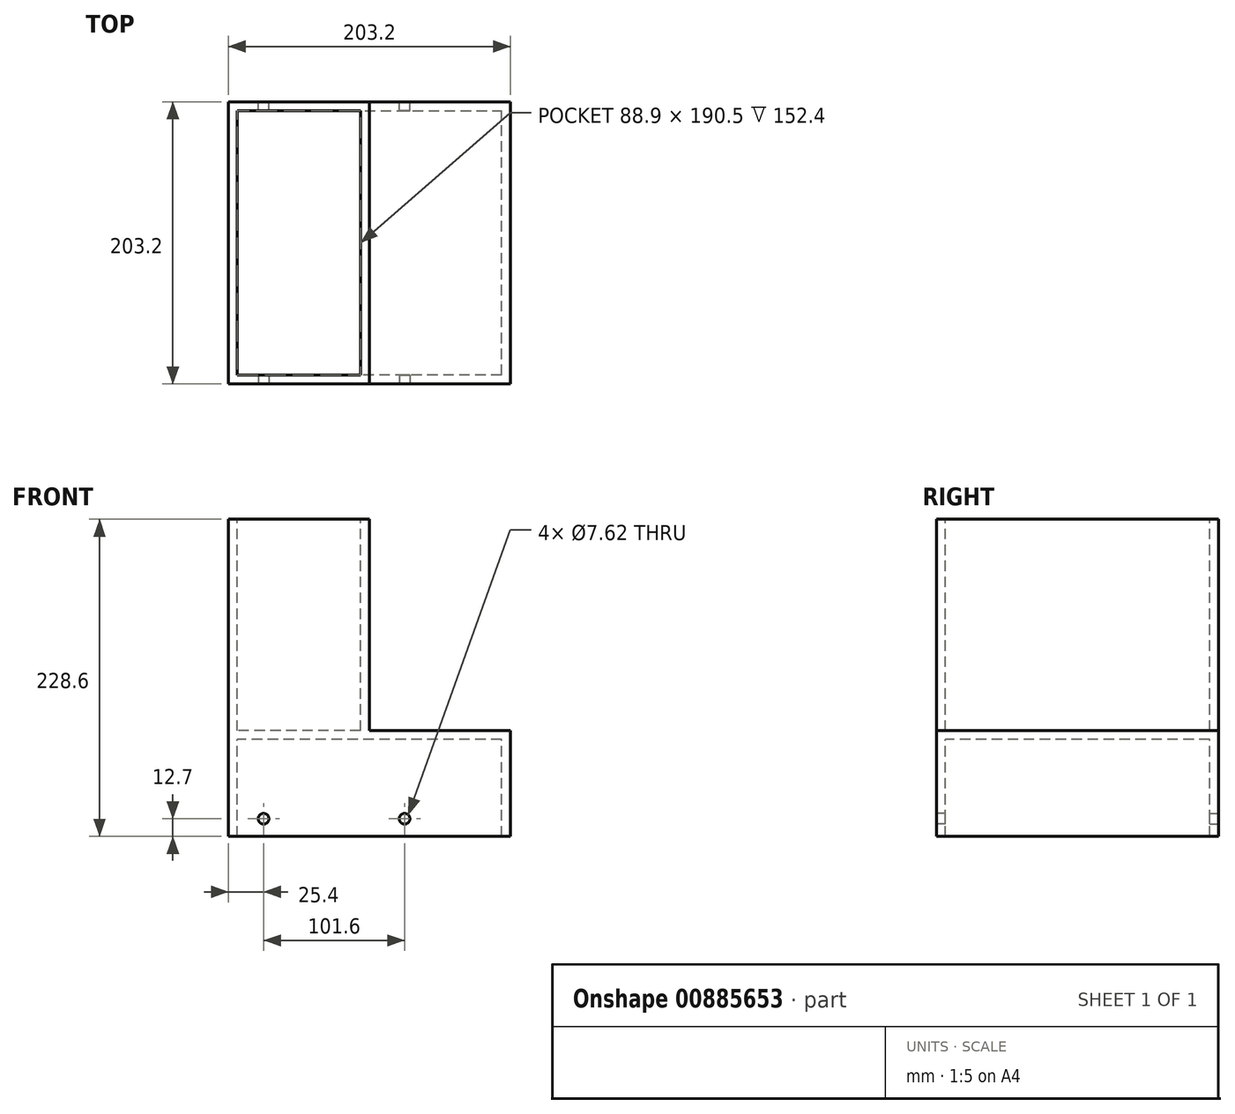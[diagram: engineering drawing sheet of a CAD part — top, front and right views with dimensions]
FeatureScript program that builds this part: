
annotation { "Feature Type Name" : "Feature", "Feature Type Description" : "" }
export const myFeature = defineFeature(function(context is Context, id is Id, definition is map)
    precondition{}
    {
        {
            var Q0;
            Q0=qCreatedBy(makeId("Front.planeOp"),FACE);
            var sketch = newSketch(context, id + "F0", { "sketchPlane" : qUnion([Q0])});
            skLineSegment(sketch, "E0.top", {"start": v(0, 152.4) * mm, "end": v(-101.6, 152.4) * mm});
            skLineSegment(sketch, "E0.left", {"start": v(0, 0) * mm, "end": v(0, 152.4) * mm});
            skLineSegment(sketch, "E0.right", {"start": v(-101.6, 0) * mm, "end": v(-101.6, 152.4) * mm});
            skLineSegment(sketch, "E1", {"start": v(-101.6, 0) * mm, "end": v(-101.6, -76.2) * mm});
            skLineSegment(sketch, "E2", {"start": v(-101.6, -76.2) * mm, "end": v(101.6, -76.2) * mm});
            skLineSegment(sketch, "E3", {"start": v(101.6, -76.2) * mm, "end": v(101.6, 0) * mm});
            skLineSegment(sketch, "E4", {"start": v(101.6, 0) * mm, "end": v(0, 0) * mm});
            skSolve(sketch);
        }
        {
            var Q0;
            Q0=qSketchRegion(id+"F0",true);
            extrude(context, id + "F1", {"entities" : qUnion([Q0]), "depth" : 101.6 * mm, "offsetDistance" : 25.4 * mm});
        }
        {
            var Q0;
            Q0=makeQuery(id+"F1.opExtrude","SWEPT_FACE",FACE,{"disambiguationData":[OSD([sQuery(id+"F0.wireOp",EDGE,"E0.top")])]});
            var Q1;
            Q1=makeQuery(id+"F1.opExtrude","CAP_FACE",FACE,{"disambiguationData":[OSD([sQuery(id+"F0.wireOp",EDGE,"E0.bottom"),sQuery(id+"F0.wireOp",EDGE,"E0.top"),sQuery(id+"F0.wireOp",EDGE,"E0.left"),sQuery(id+"F0.wireOp",EDGE,"E0.right")])],"isStart":true});
            var Q2;
            Q2=makeQuery(id+"F1.opExtrude","SWEPT_FACE",FACE,{"disambiguationData":[OSD([sQuery(id+"F0.wireOp",EDGE,"E2")])]});
            shell(context, id + "F2", {"entities" : qUnion([Q0, Q1, Q2]), "thickness" : 6.35 * mm});
        }
        {
            var Q0;
            {var subQ0=sQuery(id+"F0.wireOp",EDGE,"E4");var subQ1=sQuery(id+"F0.wireOp",EDGE,"E3");var subQ2=sQuery(id+"F0.wireOp",EDGE,"E2");var subQ3=sQuery(id+"F0.wireOp",EDGE,"E1");var subQ4=sQuery(id+"F0.wireOp",EDGE,"E0.right");var subQ5=sQuery(id+"F0.wireOp",EDGE,"E0.left");var subQ6=sQuery(id+"F0.wireOp",EDGE,"E0.top");Q0=makeQuery(id+"F2.opShell","OFFSET_FACE",FACE,{"disambiguationData":[OSD([subQ6,subQ5,subQ4,subQ3,subQ2,subQ1,subQ0]),TDD([makeQuery(id+"F1.opExtrude","CAP_FACE",FACE,{"disambiguationData":[OSD([subQ6,subQ5,subQ4,subQ3,subQ2,subQ1,subQ0])],"isStart":false})])]});}
            var sketch = newSketch(context, id + "F3", { "sketchPlane" : qUnion([Q0])});
            skLineSegment(sketch, "E5.bottom", {"start": v(6.35, 0) * mm, "end": v(95.25, 0) * mm});
            skLineSegment(sketch, "E5.top", {"start": v(6.35, -6.35) * mm, "end": v(95.25, -6.35) * mm});
            skLineSegment(sketch, "E5.left", {"start": v(6.35, -6.35) * mm, "end": v(6.35, 0) * mm});
            skLineSegment(sketch, "E5.right", {"start": v(95.25, -6.35) * mm, "end": v(95.25, 0) * mm});
            skSolve(sketch);
        }
        {
            var Q0;
            Q0=makeQuery(id+"F3.imprint","IMPRINT",FACE,{"disambiguationData":[TD([[makeQuery(id+"F3.imprint","IMPRINT",EDGE,{"derivedFrom":sQuery(id+"F3.wireOp",EDGE,"E5.bottom")}),-1.0]])]});
            extrude(context, id + "F4", {"entities" : qUnion([Q0]), "operationType" : NewBodyOperationType.ADD, "depth" : 95.25 * mm, "offsetDistance" : 25.4 * mm});
        }
        {
            var Q0;
            Q0=makeQuery(id+"F8.boolean.opBoolean","MERGE",FACE,{"derivedFrom":[makeQuery(id+"F1.opExtrude","CAP_FACE",FACE,{"disambiguationData":[OSD([sQuery(id+"F0.wireOp",EDGE,"E0.top"),sQuery(id+"F0.wireOp",EDGE,"E0.left"),sQuery(id+"F0.wireOp",EDGE,"E0.right"),sQuery(id+"F0.wireOp",EDGE,"E1"),sQuery(id+"F0.wireOp",EDGE,"E2"),sQuery(id+"F0.wireOp",EDGE,"E3"),sQuery(id+"F0.wireOp",EDGE,"E4")])],"isStart":false}),makeQuery(id+"F8.opExtrude","SWEPT_FACE",FACE,{"disambiguationData":[OSD([sQuery(id+"FagyflPpCQftM70_1.wireOp",EDGE,"fLGZwNDE-wJ8r-skwH-z4Tb-utK9fmcBo4cX.top")])]})]});
            var sketch = newSketch(context, id + "F5", { "sketchPlane" : qUnion([Q0])});
            skCircle(sketch, "E6", {"center": v(-76.2, -63.5) * mm, "radius": 3.81 * mm});
            skCircle(sketch, "E7", {"center": v(25.4, -63.5) * mm, "radius": 3.81 * mm});
            skSolve(sketch);
        }
        {
            var Q0;
            Q0 = qSketchRegion(id + "F5", true);
            extrude(context, id + "F6", {"entities" : qUnion([Q0]), "operationType" : NewBodyOperationType.REMOVE, "oppositeDirection" : true, "depth" : 25.4 * mm, "offsetDistance" : 25.4 * mm});
        }
        {
            var Q0;
            Q0=makeQuery(id+"F1.opExtrude","SWEPT_BODY",BODY,{"disambiguationData":[OSD([sQuery(id+"F0.wireOp",EDGE,"E0.bottom"),sQuery(id+"F0.wireOp",EDGE,"E0.top"),sQuery(id+"F0.wireOp",EDGE,"E0.left"),sQuery(id+"F0.wireOp",EDGE,"E0.right")])]});
            var Q1;
            Q1=makeQuery(id+"F1.opExtrude","CAP_FACE",FACE,{"disambiguationData":[OSD([sQuery(id+"F0.wireOp",EDGE,"E0.bottom"),sQuery(id+"F0.wireOp",EDGE,"E0.top"),sQuery(id+"F0.wireOp",EDGE,"E0.left"),sQuery(id+"F0.wireOp",EDGE,"E0.right")])],"isStart":true});
            mirror(context, id + "F7", {"operationType" : NewBodyOperationType.ADD, "entities" : qUnion([Q0]), "mirrorPlane" : qUnion([Q1])});
        }
    });
